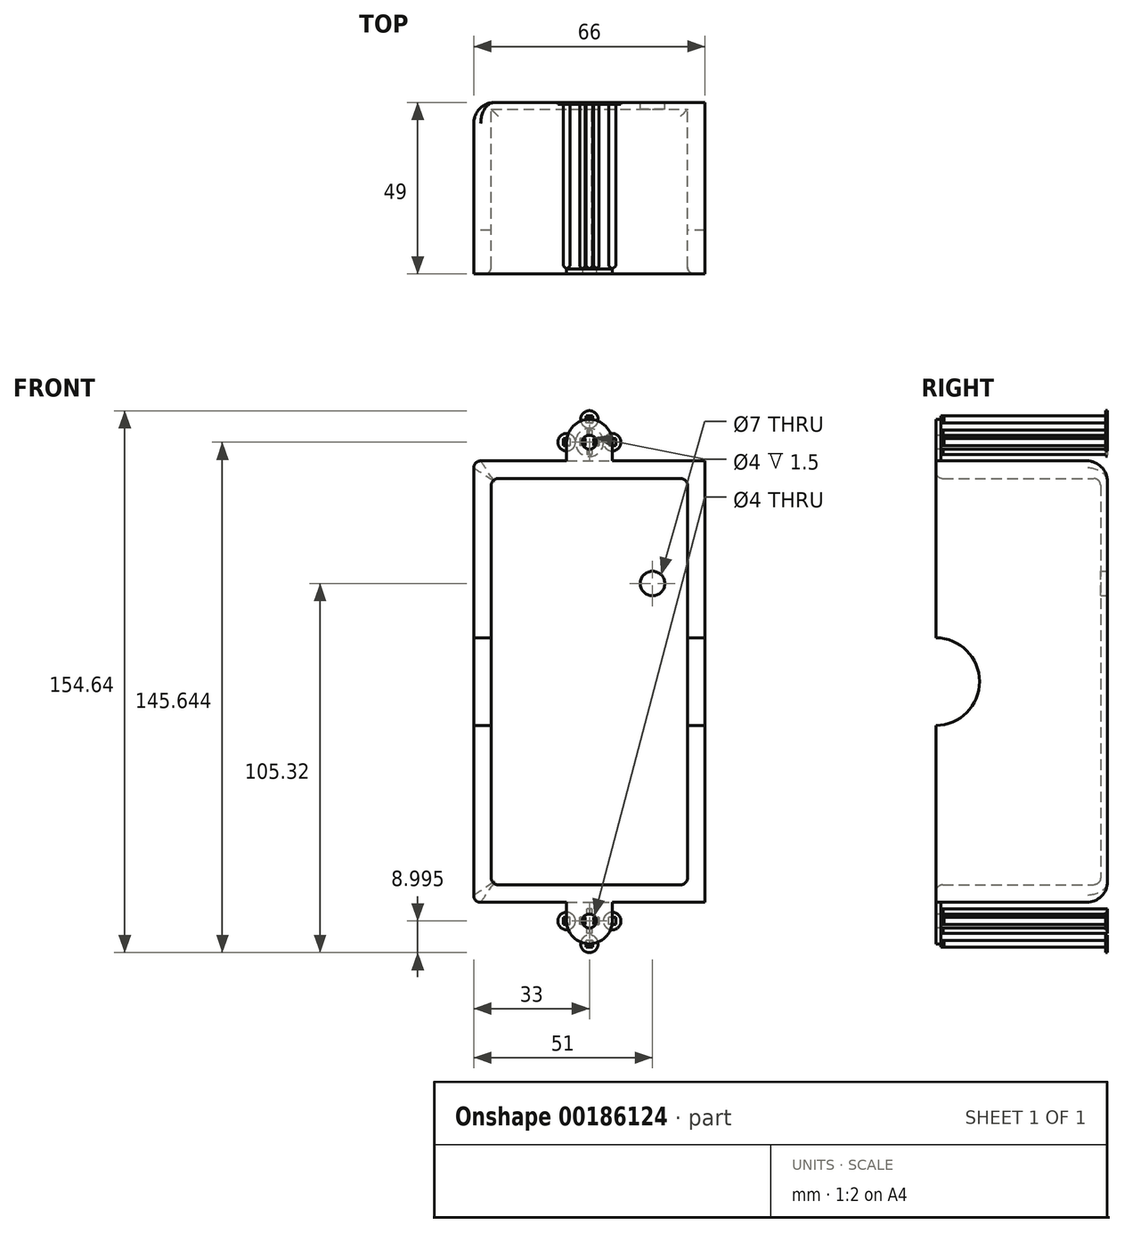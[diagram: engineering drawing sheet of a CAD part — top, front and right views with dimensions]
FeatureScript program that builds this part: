
annotation { "Feature Type Name" : "Feature", "Feature Type Description" : "" }
export const myFeature = defineFeature(function(context is Context, id is Id, definition is map)
    precondition{}
    {
        {
            var Q0;
            Q0=qCreatedBy(makeId("Front.planeOp"),FACE);
            var sketch = newSketch(context, id + "F0", { "sketchPlane" : qUnion([Q0])});
            skLineSegment(sketch, "E0.bottom", {"start": v(-33, 63) * mm, "end": v(33, 63) * mm});
            skLineSegment(sketch, "E0.top", {"start": v(-33, -63) * mm, "end": v(33, -63) * mm});
            skLineSegment(sketch, "E0.left", {"start": v(-33, 63) * mm, "end": v(-33, -63) * mm});
            skLineSegment(sketch, "E0.right", {"start": v(33, 63) * mm, "end": v(33, -63) * mm});
            skPoint(sketch, "E1", {"position": v(0, 63) * mm});
            skPoint(sketch, "E2", {"position": v(0, -63) * mm});
            skPoint(sketch, "E3", {"position": v(33, 0) * mm});
            skPoint(sketch, "E4", {"position": v(-33, 0) * mm});
            skLineSegment(sketch, "E5.bottom", {"start": v(-28, 58) * mm, "end": v(28, 58) * mm});
            skLineSegment(sketch, "E5.top", {"start": v(-28, -58) * mm, "end": v(28, -58) * mm});
            skLineSegment(sketch, "E5.left", {"start": v(-28, 58) * mm, "end": v(-28, -58) * mm});
            skLineSegment(sketch, "E5.right", {"start": v(28, 58) * mm, "end": v(28, -58) * mm});
            skPoint(sketch, "E6", {"position": v(0, 58) * mm});
            skPoint(sketch, "E7", {"position": v(28, 0) * mm});
            skCircle(sketch, "E8", {"center": v(18, 28) * mm, "radius": 3.5 * mm});
            skSolve(sketch);
        }
        {
            var Q0;
            Q0=makeQuery(id+"F0.imprint","IMPRINT",FACE,{"disambiguationData":[TD([[makeQuery(id+"F0.imprint","IMPRINT",EDGE,{"derivedFrom":sQuery(id+"F0.wireOp",EDGE,"E0.bottom")}),-1.0]])]});
            extrude(context, id + "F1", {"entities" : qUnion([Q0]), "depth" : 49 * mm});
        }
        {
            var Q0;
            Q0=makeQuery(id+"F0.imprint","IMPRINT",FACE,{"disambiguationData":[TD([[makeQuery(id+"F0.imprint","IMPRINT",EDGE,{"derivedFrom":sQuery(id+"F0.wireOp",EDGE,"E5.bottom")}),-1.0]])]});
            extrude(context, id + "F2", {"entities" : qUnion([Q0]), "operationType" : NewBodyOperationType.ADD, "depth" : 2 * mm});
        }
        {
            var Q0;
            Q0=makeQuery(id+"F1.opExtrude","CAP_EDGE",EDGE,{"disambiguationData":[OSD([sQuery(id+"F0.wireOp",EDGE,"E0.bottom")])],"isStart":true});
            var Q1;
            Q1=makeQuery(id+"F1.opExtrude","CAP_EDGE",EDGE,{"disambiguationData":[OSD([sQuery(id+"F0.wireOp",EDGE,"E0.left")])],"isStart":true});
            var Q2;
            Q2=makeQuery(id+"F1.opExtrude","CAP_EDGE",EDGE,{"disambiguationData":[OSD([sQuery(id+"F0.wireOp",EDGE,"E0.top")])],"isStart":true});
            fillet(context, id + "F3", {"entities" : qUnion([Q0, Q1, Q2]), "radius" : 6 * mm, "tangentPropagation" : true, "allowEdgeOverflow" : false});
        }
        {
            var Q0;
            Q0=makeQuery(id+"F1.opExtrude","CAP_EDGE",EDGE,{"disambiguationData":[OSD([sQuery(id+"F0.wireOp",EDGE,"E5.left")])],"isStart":false});
            var Q1;
            Q1=makeQuery(id+"F1.opExtrude","CAP_EDGE",EDGE,{"disambiguationData":[OSD([sQuery(id+"F0.wireOp",EDGE,"E5.right")])],"isStart":false});
            var Q2;
            Q2=makeQuery(id+"F1.opExtrude","CAP_EDGE",EDGE,{"disambiguationData":[OSD([sQuery(id+"F0.wireOp",EDGE,"E5.top")])],"isStart":false});
            var Q3;
            Q3=makeQuery(id+"F1.opExtrude","CAP_EDGE",EDGE,{"disambiguationData":[OSD([sQuery(id+"F0.wireOp",EDGE,"E5.bottom")])],"isStart":false});
            var Q4;
            Q4=makeQuery(id+"F1.opExtrude","SWEPT_FACE",FACE,{"disambiguationData":[OSD([sQuery(id+"F0.wireOp",EDGE,"E5.bottom")])]});
            var Q5;
            Q5=makeQuery(id+"F1.opExtrude","SWEPT_FACE",FACE,{"disambiguationData":[OSD([sQuery(id+"F0.wireOp",EDGE,"E5.top")])]});
            fillet(context, id + "F4", {"entities" : qUnion([Q0, Q1, Q2, Q3, Q4, Q5]), "radius" : 2 * mm, "tangentPropagation" : true, "allowEdgeOverflow" : false});
        }
        {
            var Q0;
            Q0=makeQuery(id+"F1.opExtrude","SWEPT_EDGE",EDGE,{"disambiguationData":[OSD([sQuery(id+"F0.wireOp",EDGE,"E0.bottom"),sQuery(id+"F0.wireOp",EDGE,"E0.left")])]});
            var Q1;
            Q1=makeQuery(id+"F1.opExtrude","SWEPT_EDGE",EDGE,{"disambiguationData":[OSD([sQuery(id+"F0.wireOp",EDGE,"E0.top"),sQuery(id+"F0.wireOp",EDGE,"E0.left")])]});
            fillet(context, id + "F5", {"entities" : qUnion([Q0, Q1]), "radius" : 2 * mm, "tangentPropagation" : true, "allowEdgeOverflow" : false});
        }
        {
            var Q0;
            Q0=makeQuery(id+"F4.opFillet","SPLIT",FACE,{"disambiguationData":[OD(1.0)],"derivedFrom":makeQuery(id+"F1.opExtrude","CAP_FACE",FACE,{"disambiguationData":[OSD([sQuery(id+"F0.wireOp",EDGE,"E0.bottom"),sQuery(id+"F0.wireOp",EDGE,"E0.top"),sQuery(id+"F0.wireOp",EDGE,"E0.left"),sQuery(id+"F0.wireOp",EDGE,"E0.right"),sQuery(id+"F0.wireOp",EDGE,"E5.bottom"),sQuery(id+"F0.wireOp",EDGE,"E5.top"),sQuery(id+"F0.wireOp",EDGE,"E5.left"),sQuery(id+"F0.wireOp",EDGE,"E5.right")])],"isStart":false})});
            var sketch = newSketch(context, id + "F6", { "sketchPlane" : qUnion([Q0])});
            skCircle(sketch, "E9", {"center": v(0, 68.32) * mm, "radius": 2 * mm});
            skLineSegment(sketch, "E10", {"start": v(6.5, 68.32) * mm, "end": v(6.5, 63) * mm});
            skLineSegment(sketch, "E11.MirrorCS", {"start": v(-6.5, 68.32) * mm, "end": v(-6.5, 63) * mm});
            skArc(sketch, "E12", {"start": v(6.5, 68.32) * mm, "mid": v(0, 74.82) * mm, "end": v(-6.5, 68.32) * mm});
            skLineSegment(sketch, "E13", {"start": v(-6.5, 63) * mm, "end": v(6.5, 63) * mm});
            skArc(sketch, "E14.MirrorCS", {"start": v(6.5, -68.32) * mm, "mid": v(0, -74.82) * mm, "end": v(-6.5, -68.32) * mm});
            skLineSegment(sketch, "E15.MirrorCS", {"start": v(6.5, -68.32) * mm, "end": v(6.5, -63) * mm});
            skLineSegment(sketch, "E16.MirrorCS", {"start": v(-6.5, -68.32) * mm, "end": v(-6.5, -63) * mm});
            skLineSegment(sketch, "E17.MirrorCS", {"start": v(-6.5, -63) * mm, "end": v(6.5, -63) * mm});
            skCircle(sketch, "E18.MirrorC", {"center": v(0, -68.32) * mm, "radius": 2 * mm});
            skSolve(sketch);
        }
        {
            var Q0;
            Q0 = qSketchRegion(id + "F6", true);
            extrude(context, id + "F7", {"entities" : qUnion([Q0]), "operationType" : NewBodyOperationType.ADD, "oppositeDirection" : true, "depth" : 1.5 * mm});
        }
        {
            var Q0;
            Q0=makeQuery(id+"F1.opExtrude","SWEPT_FACE",FACE,{"disambiguationData":[OSD([sQuery(id+"F0.wireOp",EDGE,"E0.left")])]});
            var sketch = newSketch(context, id + "F8", { "sketchPlane" : qUnion([Q0])});
            skCircle(sketch, "E19", {"center": v(49, 0) * mm, "radius": 12.5 * mm});
            skSolve(sketch);
        }
        {
            var Q0;
            Q0 = qSketchRegion(id + "F8", true);
            extrude(context, id + "F9", {"entities" : qUnion([Q0]), "operationType" : NewBodyOperationType.REMOVE, "oppositeDirection" : true, "depth" : 70 * mm});
        }
        {
            var Q0;
            Q0=makeQuery(id+"F0.imprint","IMPRINT",FACE,{"disambiguationData":[TD([[makeQuery(id+"F0.imprint","IMPRINT",EDGE,{"derivedFrom":sQuery(id+"F0.wireOp",EDGE,"E5.bottom")}),-1.0]])]});
            var sketch = newSketch(context, id + "F10", { "sketchPlane" : qUnion([Q0])});
            skLineSegment(sketch, "E20.bottom", {"start": v(7.5, 69.32) * mm, "end": v(5.5, 69.32) * mm});
            skLineSegment(sketch, "E20.top", {"start": v(7.5, 67.32) * mm, "end": v(5.5, 67.32) * mm});
            skLineSegment(sketch, "E20.left", {"start": v(7.5, 69.32) * mm, "end": v(7.5, 67.32) * mm});
            skLineSegment(sketch, "E20.right", {"start": v(5.5, 69.32) * mm, "end": v(5.5, 67.32) * mm});
            skPoint(sketch, "E21", {"position": v(6.5, 69.32) * mm});
            skLineSegment(sketch, "E22.MirrorCS", {"start": v(-7.5, 69.32) * mm, "end": v(-5.5, 69.32) * mm});
            skLineSegment(sketch, "E23.MirrorCS", {"start": v(-7.5, 69.32) * mm, "end": v(-7.5, 67.32) * mm});
            skLineSegment(sketch, "E24.MirrorCS", {"start": v(-7.5, 67.32) * mm, "end": v(-5.5, 67.32) * mm});
            skLineSegment(sketch, "E25.MirrorCS", {"start": v(-5.5, 69.32) * mm, "end": v(-5.5, 67.32) * mm});
            skLineSegment(sketch, "E26.bottom", {"start": v(1, 75.82) * mm, "end": v(-1, 75.82) * mm});
            skLineSegment(sketch, "E26.top", {"start": v(1, 73.82) * mm, "end": v(-1, 73.82) * mm});
            skLineSegment(sketch, "E26.left", {"start": v(1, 75.82) * mm, "end": v(1, 73.82) * mm});
            skLineSegment(sketch, "E26.right", {"start": v(-1, 75.82) * mm, "end": v(-1, 73.82) * mm});
            skPoint(sketch, "E27", {"position": v(0, 75.82) * mm});
            skLineSegment(sketch, "E28.MirrorCS", {"start": v(-5.5, -69.32) * mm, "end": v(-5.5, -67.32) * mm});
            skLineSegment(sketch, "E29.MirrorCS", {"start": v(-7.5, -67.32) * mm, "end": v(-5.5, -67.32) * mm});
            skLineSegment(sketch, "E30.MirrorCS", {"start": v(-7.5, -69.32) * mm, "end": v(-7.5, -67.32) * mm});
            skLineSegment(sketch, "E31.MirrorCS", {"start": v(-7.5, -69.32) * mm, "end": v(-5.5, -69.32) * mm});
            skLineSegment(sketch, "E32.MirrorCS", {"start": v(1, -73.82) * mm, "end": v(-1, -73.82) * mm});
            skLineSegment(sketch, "E33.MirrorCS", {"start": v(-1, -75.82) * mm, "end": v(-1, -73.82) * mm});
            skLineSegment(sketch, "E34.MirrorCS", {"start": v(1, -75.82) * mm, "end": v(-1, -75.82) * mm});
            skLineSegment(sketch, "E35.MirrorCS", {"start": v(1, -75.82) * mm, "end": v(1, -73.82) * mm});
            skLineSegment(sketch, "E36.MirrorCS", {"start": v(5.5, -69.32) * mm, "end": v(5.5, -67.32) * mm});
            skLineSegment(sketch, "E37.MirrorCS", {"start": v(7.5, -67.32) * mm, "end": v(5.5, -67.32) * mm});
            skLineSegment(sketch, "E38.MirrorCS", {"start": v(7.5, -69.32) * mm, "end": v(5.5, -69.32) * mm});
            skLineSegment(sketch, "E39.MirrorCS", {"start": v(7.5, -69.32) * mm, "end": v(7.5, -67.32) * mm});
            skCircle(sketch, "E40", {"center": v(-6.5, -68.32) * mm, "radius": 2.5 * mm});
            skCircle(sketch, "E41", {"center": v(6.5, -68.32) * mm, "radius": 2.5 * mm});
            skPoint(sketch, "E41.centerSnap0", {"position": v(6.5, -67.32) * mm});
            skCircle(sketch, "E42", {"center": v(0, -74.82) * mm, "radius": 2.5 * mm});
            skCircle(sketch, "E43.MirrorC", {"center": v(-6.5, 68.32) * mm, "radius": 2.5 * mm});
            skCircle(sketch, "E44.MirrorC", {"center": v(6.5, 68.32) * mm, "radius": 2.5 * mm});
            skCircle(sketch, "E45.MirrorC", {"center": v(0, 74.82) * mm, "radius": 2.5 * mm});
            skLineSegment(sketch, "E46.bottom", {"start": v(0.75, 71.82) * mm, "end": v(-0.75, 71.82) * mm});
            skLineSegment(sketch, "E46.top", {"start": v(0.75, 70.32) * mm, "end": v(-0.75, 70.32) * mm});
            skLineSegment(sketch, "E46.left", {"start": v(0.75, 71.82) * mm, "end": v(0.75, 70.32) * mm});
            skLineSegment(sketch, "E46.right", {"start": v(-0.75, 71.82) * mm, "end": v(-0.75, 70.32) * mm});
            skPoint(sketch, "E47", {"position": v(0, 70.32) * mm});
            skLineSegment(sketch, "E48.bottom", {"start": v(0.75, 66.32) * mm, "end": v(-0.75, 66.32) * mm});
            skLineSegment(sketch, "E48.top", {"start": v(0.75, 64.82) * mm, "end": v(-0.75, 64.82) * mm});
            skLineSegment(sketch, "E48.left", {"start": v(0.75, 66.32) * mm, "end": v(0.75, 64.82) * mm});
            skLineSegment(sketch, "E48.right", {"start": v(-0.75, 66.32) * mm, "end": v(-0.75, 64.82) * mm});
            skPoint(sketch, "E49", {"position": v(0, 66.32) * mm});
            skLineSegment(sketch, "E50.bottom", {"start": v(-1.25, 69.32) * mm, "end": v(-2.75, 69.32) * mm});
            skLineSegment(sketch, "E50.top", {"start": v(-1.25, 67.32) * mm, "end": v(-2.75, 67.32) * mm});
            skLineSegment(sketch, "E50.left", {"start": v(-1.25, 69.32) * mm, "end": v(-1.25, 67.32) * mm});
            skLineSegment(sketch, "E50.right", {"start": v(-2.75, 69.32) * mm, "end": v(-2.75, 67.32) * mm});
            skPoint(sketch, "E51", {"position": v(-2, 69.32) * mm});
            skPoint(sketch, "E52", {"position": v(-1.25, 68.32) * mm});
            skLineSegment(sketch, "E53.MirrorCS", {"start": v(1.25, 69.32) * mm, "end": v(2.75, 69.32) * mm});
            skLineSegment(sketch, "E54.MirrorCS", {"start": v(1.25, 69.32) * mm, "end": v(1.25, 67.32) * mm});
            skLineSegment(sketch, "E55.MirrorCS", {"start": v(2.75, 69.32) * mm, "end": v(2.75, 67.32) * mm});
            skLineSegment(sketch, "E56.MirrorCS", {"start": v(1.25, 67.32) * mm, "end": v(2.75, 67.32) * mm});
            skCircle(sketch, "E57", {"center": v(0, 68.26) * mm, "radius": 4 * mm});
            skCircle(sketch, "E58.MirrorC", {"center": v(0, -68.26) * mm, "radius": 4 * mm});
            skLineSegment(sketch, "E59.MirrorCS", {"start": v(0.75, -71.82) * mm, "end": v(-0.75, -71.82) * mm});
            skLineSegment(sketch, "E60.MirrorCS", {"start": v(0.75, -71.82) * mm, "end": v(0.75, -70.32) * mm});
            skLineSegment(sketch, "E61.MirrorCS", {"start": v(-0.75, -71.82) * mm, "end": v(-0.75, -70.32) * mm});
            skLineSegment(sketch, "E62.MirrorCS", {"start": v(0.75, -70.32) * mm, "end": v(-0.75, -70.32) * mm});
            skLineSegment(sketch, "E63.MirrorCS", {"start": v(1.25, -69.32) * mm, "end": v(1.25, -67.32) * mm});
            skLineSegment(sketch, "E64.MirrorCS", {"start": v(1.25, -69.32) * mm, "end": v(2.75, -69.32) * mm});
            skLineSegment(sketch, "E65.MirrorCS", {"start": v(2.75, -69.32) * mm, "end": v(2.75, -67.32) * mm});
            skLineSegment(sketch, "E66.MirrorCS", {"start": v(1.25, -67.32) * mm, "end": v(2.75, -67.32) * mm});
            skLineSegment(sketch, "E67.MirrorCS", {"start": v(0.75, -66.32) * mm, "end": v(0.75, -64.82) * mm});
            skLineSegment(sketch, "E68.MirrorCS", {"start": v(0.75, -66.32) * mm, "end": v(-0.75, -66.32) * mm});
            skLineSegment(sketch, "E69.MirrorCS", {"start": v(-0.75, -66.32) * mm, "end": v(-0.75, -64.82) * mm});
            skLineSegment(sketch, "E70.MirrorCS", {"start": v(0.75, -64.82) * mm, "end": v(-0.75, -64.82) * mm});
            skLineSegment(sketch, "E71.MirrorCS", {"start": v(-1.25, -69.32) * mm, "end": v(-1.25, -67.32) * mm});
            skLineSegment(sketch, "E72.MirrorCS", {"start": v(-1.25, -69.32) * mm, "end": v(-2.75, -69.32) * mm});
            skLineSegment(sketch, "E73.MirrorCS", {"start": v(-2.75, -69.32) * mm, "end": v(-2.75, -67.32) * mm});
            skLineSegment(sketch, "E74.MirrorCS", {"start": v(-1.25, -67.32) * mm, "end": v(-2.75, -67.32) * mm});
            skPoint(sketch, "E75", {"position": v(-2, 68.32) * mm});
            skPoint(sketch, "E76", {"position": v(2, 68.32) * mm});
            skPoint(sketch, "E76.positionSnap0", {"position": v(2, 69.32) * mm});
            skPoint(sketch, "E76.positionSnap1", {"position": v(1.25, 68.32) * mm});
            skSolve(sketch);
        }
        {
            var Q0;
            Q0=makeQuery(id+"F10.imprint","IMPRINT",FACE,{"disambiguationData":[TD([[makeQuery(id+"F10.imprint","IMPRINT",EDGE,{"derivedFrom":sQuery(id+"F10.wireOp",EDGE,"E32.MirrorCS")}),1.0]])]});
            var Q1;
            Q1=makeQuery(id+"F10.imprint","IMPRINT",FACE,{"disambiguationData":[TD([[makeQuery(id+"F10.imprint","IMPRINT",EDGE,{"derivedFrom":sQuery(id+"F10.wireOp",EDGE,"E36.MirrorCS")}),-1.0]])]});
            var Q2;
            Q2=makeQuery(id+"F10.imprint","IMPRINT",FACE,{"disambiguationData":[TD([[makeQuery(id+"F10.imprint","IMPRINT",EDGE,{"derivedFrom":sQuery(id+"F10.wireOp",EDGE,"E28.MirrorCS")}),1.0]])]});
            var Q3;
            Q3=makeQuery(id+"F10.imprint","IMPRINT",FACE,{"disambiguationData":[TD([[makeQuery(id+"F10.imprint","IMPRINT",EDGE,{"derivedFrom":sQuery(id+"F10.wireOp",EDGE,"E22.MirrorCS")}),-1.0]])]});
            var Q4;
            Q4=makeQuery(id+"F10.imprint","IMPRINT",FACE,{"disambiguationData":[TD([[makeQuery(id+"F10.imprint","IMPRINT",EDGE,{"derivedFrom":sQuery(id+"F10.wireOp",EDGE,"E26.bottom")}),1.0]])]});
            var Q5;
            Q5=makeQuery(id+"F10.imprint","IMPRINT",FACE,{"disambiguationData":[TD([[makeQuery(id+"F10.imprint","IMPRINT",EDGE,{"derivedFrom":sQuery(id+"F10.wireOp",EDGE,"E20.bottom")}),1.0]])]});
            var Q6;
            Q6=makeQuery(id+"F10.imprint","IMPRINT",FACE,{"disambiguationData":[TD([[makeQuery(id+"F10.imprint","IMPRINT",EDGE,{"derivedFrom":sQuery(id+"F10.wireOp",EDGE,"E46.bottom")}),1.0]])]});
            var Q7;
            Q7=makeQuery(id+"F10.imprint","IMPRINT",FACE,{"disambiguationData":[TD([[makeQuery(id+"F10.imprint","IMPRINT",EDGE,{"derivedFrom":sQuery(id+"F10.wireOp",EDGE,"E53.MirrorCS")}),-1.0]])]});
            var Q8;
            Q8=makeQuery(id+"F10.imprint","IMPRINT",FACE,{"disambiguationData":[TD([[makeQuery(id+"F10.imprint","IMPRINT",EDGE,{"derivedFrom":sQuery(id+"F10.wireOp",EDGE,"E48.bottom")}),1.0]])]});
            var Q9;
            Q9=makeQuery(id+"F10.imprint","IMPRINT",FACE,{"disambiguationData":[TD([[makeQuery(id+"F10.imprint","IMPRINT",EDGE,{"derivedFrom":sQuery(id+"F10.wireOp",EDGE,"E50.bottom")}),1.0]])]});
            var Q10;
            Q10=makeQuery(id+"F10.imprint","IMPRINT",FACE,{"disambiguationData":[TD([[makeQuery(id+"F10.imprint","IMPRINT",EDGE,{"derivedFrom":sQuery(id+"F10.wireOp",EDGE,"E67.MirrorCS")}),1.0]])]});
            var Q11;
            Q11=makeQuery(id+"F10.imprint","IMPRINT",FACE,{"disambiguationData":[TD([[makeQuery(id+"F10.imprint","IMPRINT",EDGE,{"derivedFrom":sQuery(id+"F10.wireOp",EDGE,"E63.MirrorCS")}),-1.0]])]});
            var Q12;
            Q12=makeQuery(id+"F10.imprint","IMPRINT",FACE,{"disambiguationData":[TD([[makeQuery(id+"F10.imprint","IMPRINT",EDGE,{"derivedFrom":sQuery(id+"F10.wireOp",EDGE,"E59.MirrorCS")}),-1.0]])]});
            var Q13;
            Q13=makeQuery(id+"F10.imprint","IMPRINT",FACE,{"disambiguationData":[TD([[makeQuery(id+"F10.imprint","IMPRINT",EDGE,{"derivedFrom":sQuery(id+"F10.wireOp",EDGE,"E71.MirrorCS")}),1.0]])]});
            extrude(context, id + "F11", {"entities" : qUnion([Q0, Q1, Q2, Q3, Q4, Q5, Q6, Q7, Q8, Q9, Q10, Q11, Q12, Q13]), "operationType" : NewBodyOperationType.ADD, "depth" : 47.5 * mm});
        }
        {
            var Q0;
            Q0=makeQuery(id+"F11.opExtrude","SWEPT_FACE",FACE,{"disambiguationData":[OSD([sQuery(id+"F10.wireOp",EDGE,"E20.bottom")])]});
            var sketch = newSketch(context, id + "F12", { "sketchPlane" : qUnion([Q0])});
            skLineSegment(sketch, "E77", {"start": v(7.5, -46.69) * mm, "end": v(6.5, -47.5) * mm});
            skLineSegment(sketch, "E78", {"start": v(5.5, -46.69) * mm, "end": v(6.4, -47.5) * mm});
            skLineSegment(sketch, "E79", {"start": v(6.4, -47.5) * mm, "end": v(5.5, -47.5) * mm});
            skLineSegment(sketch, "E80", {"start": v(5.5, -47.5) * mm, "end": v(5.5, -46.69) * mm});
            skLineSegment(sketch, "E81", {"start": v(6.5, -47.5) * mm, "end": v(7.5, -47.5) * mm});
            skLineSegment(sketch, "E82", {"start": v(7.5, -47.5) * mm, "end": v(7.5, -46.69) * mm});
            skPoint(sketch, "E83", {"position": v(6.96, -47.5) * mm});
            skLineSegment(sketch, "E84.MirrorCS", {"start": v(-5.5, -46.69) * mm, "end": v(-6.4, -47.5) * mm});
            skLineSegment(sketch, "E85.MirrorCS", {"start": v(-6.4, -47.5) * mm, "end": v(-5.5, -47.5) * mm});
            skLineSegment(sketch, "E86.MirrorCS", {"start": v(-5.5, -47.5) * mm, "end": v(-5.5, -46.69) * mm});
            skLineSegment(sketch, "E87.MirrorCS", {"start": v(-6.5, -47.5) * mm, "end": v(-7.5, -47.5) * mm});
            skLineSegment(sketch, "E88.MirrorCS", {"start": v(-7.5, -47.5) * mm, "end": v(-7.5, -46.69) * mm});
            skLineSegment(sketch, "E89.MirrorCS", {"start": v(-7.5, -46.69) * mm, "end": v(-6.5, -47.5) * mm});
            skSolve(sketch);
        }
        {
            var Q0;
            Q0 = qSketchRegion(id + "F12", true);
            extrude(context, id + "F13", {"entities" : qUnion([Q0]), "operationType" : NewBodyOperationType.REMOVE, "oppositeDirection" : true, "depth" : 2 * mm});
        }
        {
            var Q0;
            Q0=makeQuery(id+"F11.opExtrude","SWEPT_FACE",FACE,{"disambiguationData":[OSD([sQuery(id+"F10.wireOp",EDGE,"E26.bottom")])]});
            var sketch = newSketch(context, id + "F14", { "sketchPlane" : qUnion([Q0])});
            skPoint(sketch, "E90", {"position": v(-1, -46.69) * mm});
            skLineSegment(sketch, "E91", {"start": v(-1, -46.69) * mm, "end": v(-0.03, -47.5) * mm});
            skLineSegment(sketch, "E92", {"start": v(-0.03, -47.5) * mm, "end": v(-1, -47.5) * mm});
            skLineSegment(sketch, "E93", {"start": v(-1, -47.5) * mm, "end": v(-1, -46.69) * mm});
            skLineSegment(sketch, "E94", {"start": v(1, -46.69) * mm, "end": v(0.07, -47.5) * mm});
            skLineSegment(sketch, "E95", {"start": v(0.07, -47.5) * mm, "end": v(1, -47.5) * mm});
            skLineSegment(sketch, "E96", {"start": v(1, -47.5) * mm, "end": v(1, -46.69) * mm});
            skLineSegment(sketch, "E97", {"start": v(-2.75, -46.73) * mm, "end": v(-2.05, -47.5) * mm});
            skLineSegment(sketch, "E98", {"start": v(-2.05, -47.5) * mm, "end": v(-2.75, -47.5) * mm});
            skLineSegment(sketch, "E99", {"start": v(-2.75, -47.5) * mm, "end": v(-2.75, -46.73) * mm});
            skLineSegment(sketch, "E100", {"start": v(-1.25, -46.73) * mm, "end": v(-1.95, -47.5) * mm});
            skLineSegment(sketch, "E101", {"start": v(-1.95, -47.5) * mm, "end": v(-1.25, -47.5) * mm});
            skLineSegment(sketch, "E102", {"start": v(-1.25, -47.5) * mm, "end": v(-1.25, -46.73) * mm});
            skLineSegment(sketch, "E103", {"start": v(1.25, -46.69) * mm, "end": v(2.22, -47.5) * mm});
            skLineSegment(sketch, "E104", {"start": v(2.22, -47.5) * mm, "end": v(1.25, -47.5) * mm});
            skLineSegment(sketch, "E105", {"start": v(1.25, -47.5) * mm, "end": v(1.25, -46.69) * mm});
            skLineSegment(sketch, "E106", {"start": v(2.75, -46.69) * mm, "end": v(2.32, -47.5) * mm});
            skLineSegment(sketch, "E107", {"start": v(2.32, -47.5) * mm, "end": v(2.75, -47.5) * mm});
            skLineSegment(sketch, "E108", {"start": v(2.75, -47.5) * mm, "end": v(2.75, -46.69) * mm});
            skSolve(sketch);
        }
        {
            var Q0;
            Q0 = qSketchRegion(id + "F14", true);
            extrude(context, id + "F15", {"entities" : qUnion([Q0]), "operationType" : NewBodyOperationType.REMOVE, "oppositeDirection" : true, "depth" : 12 * mm});
        }
        {
            var Q0;
            Q0=makeQuery(id+"F11.opExtrude","SWEPT_FACE",FACE,{"disambiguationData":[OSD([sQuery(id+"F10.wireOp",EDGE,"E31.MirrorCS")])]});
            var sketch = newSketch(context, id + "F16", { "sketchPlane" : qUnion([Q0])});
            skPoint(sketch, "E109", {"position": v(-7.5, 46.69) * mm});
            skPoint(sketch, "E110", {"position": v(-5.5, 46.69) * mm});
            skPoint(sketch, "E111", {"position": v(-6.5, 47.5) * mm});
            skPoint(sketch, "E112", {"position": v(-6.4, 47.5) * mm});
            skPoint(sketch, "E113", {"position": v(5.5, 46.69) * mm});
            skPoint(sketch, "E114", {"position": v(6.4, 47.5) * mm});
            skPoint(sketch, "E115", {"position": v(7.5, 46.69) * mm});
            skPoint(sketch, "E116", {"position": v(6.5, 47.5) * mm});
            skLineSegment(sketch, "E117", {"start": v(6.4, 47.5) * mm, "end": v(6.02, 47.5) * mm});
            skLineSegment(sketch, "E118", {"start": v(6.4, 47.5) * mm, "end": v(5.5, 46.69) * mm});
            skLineSegment(sketch, "E119", {"start": v(5.5, 47.5) * mm, "end": v(6.4, 47.5) * mm});
            skLineSegment(sketch, "E120", {"start": v(5.5, 47.5) * mm, "end": v(5.5, 46.69) * mm});
            skLineSegment(sketch, "E121", {"start": v(6.5, 47.5) * mm, "end": v(7.58, 47.5) * mm});
            skLineSegment(sketch, "E122", {"start": v(7.58, 47.5) * mm, "end": v(7.5, 46.69) * mm});
            skLineSegment(sketch, "E123", {"start": v(6.5, 47.5) * mm, "end": v(7.5, 46.69) * mm});
            skLineSegment(sketch, "E124", {"start": v(-7.5, 47.5) * mm, "end": v(-7.5, 46.69) * mm});
            skLineSegment(sketch, "E125", {"start": v(-6.5, 47.5) * mm, "end": v(-7.5, 47.5) * mm});
            skLineSegment(sketch, "E126", {"start": v(-7.5, 46.69) * mm, "end": v(-6.5, 47.5) * mm});
            skLineSegment(sketch, "E127", {"start": v(-6.4, 47.5) * mm, "end": v(-5.5, 46.69) * mm});
            skLineSegment(sketch, "E128", {"start": v(-6.4, 47.5) * mm, "end": v(-5.5, 47.5) * mm});
            skLineSegment(sketch, "E129", {"start": v(-5.5, 47.5) * mm, "end": v(-5.5, 46.69) * mm});
            skSolve(sketch);
        }
        {
            var Q0;
            Q0 = qSketchRegion(id + "F16", true);
            extrude(context, id + "F17", {"entities" : qUnion([Q0]), "operationType" : NewBodyOperationType.REMOVE, "oppositeDirection" : true, "depth" : 4 * mm});
        }
        {
            var Q0;
            Q0=makeQuery(id+"F11.opExtrude","SWEPT_FACE",FACE,{"disambiguationData":[OSD([sQuery(id+"F10.wireOp",EDGE,"E34.MirrorCS")])]});
            var sketch = newSketch(context, id + "F18", { "sketchPlane" : qUnion([Q0])});
            skPoint(sketch, "E130", {"position": v(-1, 46.69) * mm});
            skPoint(sketch, "E131", {"position": v(1, 46.69) * mm});
            skPoint(sketch, "E132", {"position": v(-0.03, 47.5) * mm});
            skPoint(sketch, "E133", {"position": v(0.07, 47.5) * mm});
            skPoint(sketch, "E134", {"position": v(1, 47.5) * mm});
            skPoint(sketch, "E135", {"position": v(-1, 47.5) * mm});
            skLineSegment(sketch, "E136", {"start": v(-1, 47.5) * mm, "end": v(-1, 46.69) * mm});
            skLineSegment(sketch, "E137", {"start": v(-0.03, 47.5) * mm, "end": v(-1, 47.5) * mm});
            skLineSegment(sketch, "E138", {"start": v(-0.03, 47.5) * mm, "end": v(-1, 46.69) * mm});
            skLineSegment(sketch, "E139", {"start": v(0.07, 47.5) * mm, "end": v(1, 46.69) * mm});
            skLineSegment(sketch, "E140", {"start": v(1, 47.5) * mm, "end": v(0.07, 47.5) * mm});
            skLineSegment(sketch, "E141", {"start": v(1, 47.5) * mm, "end": v(1, 46.69) * mm});
            skLineSegment(sketch, "E142", {"start": v(-1.25, 47.5) * mm, "end": v(-1, 47.5) * mm});
            skPoint(sketch, "E143", {"position": v(-1.12, 47.5) * mm});
            skLineSegment(sketch, "E144", {"start": v(-1.12, 47.5) * mm, "end": v(-1.12, 47.07) * mm});
            skLineSegment(sketch, "E145.MirrorCS", {"start": v(-2.22, 47.5) * mm, "end": v(-1.25, 46.69) * mm});
            skLineSegment(sketch, "E146.MirrorCS", {"start": v(-2.22, 47.5) * mm, "end": v(-1.25, 47.5) * mm});
            skLineSegment(sketch, "E147.MirrorCS", {"start": v(-1.25, 47.5) * mm, "end": v(-1.25, 46.69) * mm});
            skLineSegment(sketch, "E148.MirrorCS", {"start": v(-3.25, 47.5) * mm, "end": v(-2.32, 47.5) * mm});
            skLineSegment(sketch, "E149.MirrorCS", {"start": v(-2.32, 47.5) * mm, "end": v(-3.25, 46.69) * mm});
            skLineSegment(sketch, "E150.MirrorCS", {"start": v(-3.25, 47.5) * mm, "end": v(-3.25, 46.69) * mm});
            skLineSegment(sketch, "E151", {"start": v(1, 47.5) * mm, "end": v(1.25, 47.5) * mm});
            skPoint(sketch, "E152", {"position": v(1.12, 47.5) * mm});
            skLineSegment(sketch, "E153", {"start": v(1.12, 47.5) * mm, "end": v(1.12, 46.93) * mm});
            skLineSegment(sketch, "E154.MirrorCS", {"start": v(2.18, 47.5) * mm, "end": v(1.25, 46.69) * mm});
            skLineSegment(sketch, "E155.MirrorCS", {"start": v(1.25, 47.5) * mm, "end": v(2.18, 47.5) * mm});
            skLineSegment(sketch, "E156.MirrorCS", {"start": v(1.25, 47.5) * mm, "end": v(1.25, 46.69) * mm});
            skLineSegment(sketch, "E157.MirrorCS", {"start": v(2.28, 47.5) * mm, "end": v(3.25, 46.69) * mm});
            skLineSegment(sketch, "E158.MirrorCS", {"start": v(2.28, 47.5) * mm, "end": v(3.25, 47.5) * mm});
            skLineSegment(sketch, "E159.MirrorCS", {"start": v(3.25, 47.5) * mm, "end": v(3.25, 46.69) * mm});
            skSolve(sketch);
        }
        {
            var Q0;
            Q0 = qSketchRegion(id + "F18", true);
            extrude(context, id + "F19", {"entities" : qUnion([Q0]), "operationType" : NewBodyOperationType.REMOVE, "oppositeDirection" : true, "depth" : 12 * mm});
        }
        {
            var Q0;
            Q0=makeQuery(id+"F10.imprint","IMPRINT",FACE,{"disambiguationData":[TD([[makeQuery(id+"F10.imprint","IMPRINT",EDGE,{"derivedFrom":sQuery(id+"F10.wireOp",EDGE,"E26.bottom")}),-1.0]])]});
            var Q1;
            Q1=makeQuery(id+"F10.imprint","IMPRINT",FACE,{"disambiguationData":[TD([[makeQuery(id+"F10.imprint","IMPRINT",EDGE,{"derivedFrom":sQuery(id+"F10.wireOp",EDGE,"E22.MirrorCS")}),1.0]])]});
            var Q2;
            Q2=makeQuery(id+"F10.imprint","IMPRINT",FACE,{"disambiguationData":[TD([[makeQuery(id+"F10.imprint","IMPRINT",EDGE,{"derivedFrom":sQuery(id+"F10.wireOp",EDGE,"E20.bottom")}),-1.0]])]});
            var Q3;
            Q3=makeQuery(id+"F10.imprint","IMPRINT",FACE,{"disambiguationData":[TD([[makeQuery(id+"F10.imprint","IMPRINT",EDGE,{"derivedFrom":sQuery(id+"F10.wireOp",EDGE,"E32.MirrorCS")}),-1.0]])]});
            var Q4;
            Q4=makeQuery(id+"F10.imprint","IMPRINT",FACE,{"disambiguationData":[TD([[makeQuery(id+"F10.imprint","IMPRINT",EDGE,{"derivedFrom":sQuery(id+"F10.wireOp",EDGE,"E36.MirrorCS")}),1.0]])]});
            var Q5;
            Q5=makeQuery(id+"F10.imprint","IMPRINT",FACE,{"disambiguationData":[TD([[makeQuery(id+"F10.imprint","IMPRINT",EDGE,{"derivedFrom":sQuery(id+"F10.wireOp",EDGE,"E28.MirrorCS")}),-1.0]])]});
            var Q6;
            Q6=makeQuery(id+"F10.imprint","IMPRINT",FACE,{"disambiguationData":[TD([[makeQuery(id+"F10.imprint","IMPRINT",EDGE,{"derivedFrom":sQuery(id+"F10.wireOp",EDGE,"E46.bottom")}),-1.0]])]});
            var Q7;
            Q7=makeQuery(id+"F10.imprint","IMPRINT",FACE,{"disambiguationData":[TD([[makeQuery(id+"F10.imprint","IMPRINT",EDGE,{"derivedFrom":sQuery(id+"F10.wireOp",EDGE,"E58.MirrorC")}),-1.0]])]});
            extrude(context, id + "F20", {"entities" : qUnion([Q0, Q1, Q2, Q3, Q4, Q5, Q6, Q7]), "operationType" : NewBodyOperationType.ADD, "depth" : 0.5 * mm});
        }
    });
